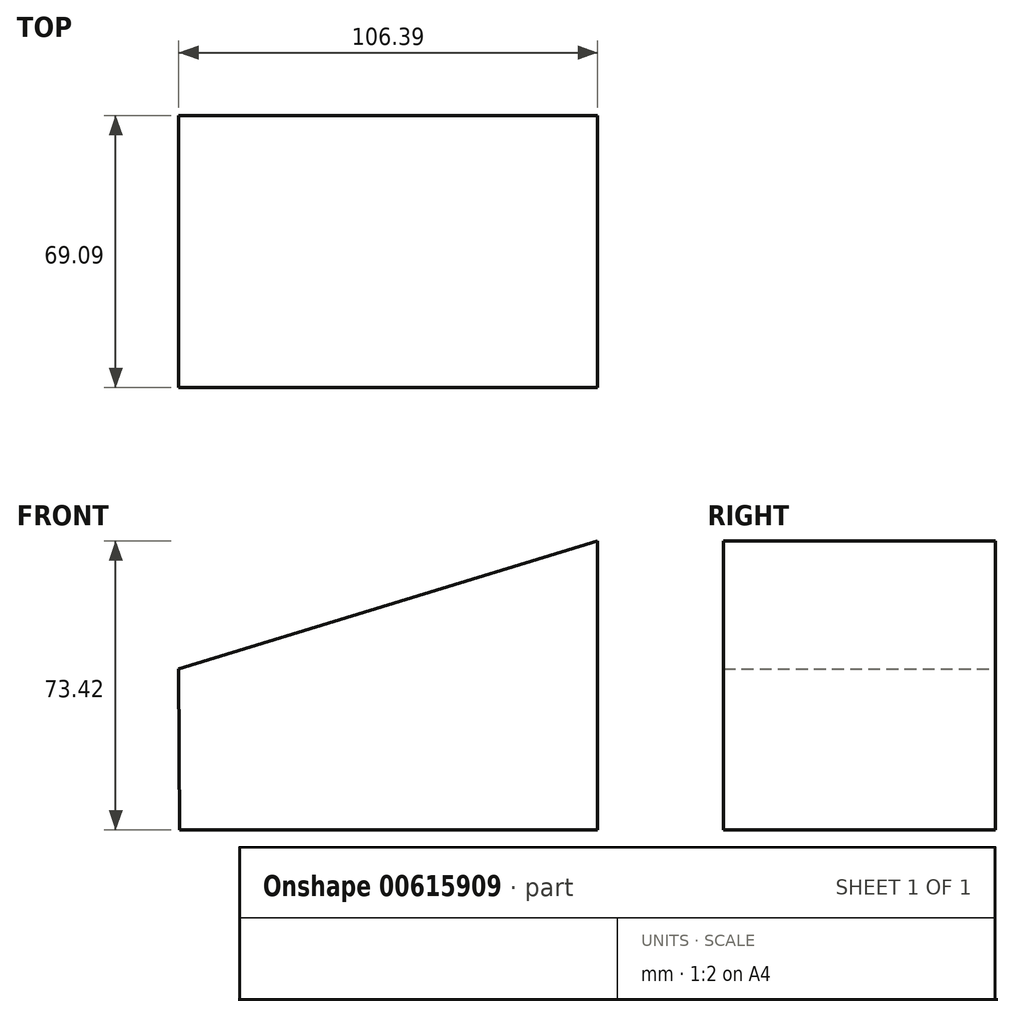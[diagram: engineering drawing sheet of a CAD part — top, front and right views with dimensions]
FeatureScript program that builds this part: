
annotation { "Feature Type Name" : "Feature", "Feature Type Description" : "" }
export const myFeature = defineFeature(function(context is Context, id is Id, definition is map)
    precondition{}
    {
        {
            var Q0;
            Q0=qCreatedBy(makeId("Front.planeOp"),FACE);
            var sketch = newSketch(context, id + "F0", { "sketchPlane" : qUnion([Q0])});
            skLineSegment(sketch, "E0", {"start": v(-59.68, 46.93) * mm, "end": v(46.7, 79.46) * mm});
            skLineSegment(sketch, "E1", {"start": v(46.7, 79.46) * mm, "end": v(46.7, 6.04) * mm});
            skLineSegment(sketch, "E2", {"start": v(46.7, 6.04) * mm, "end": v(-59.46, 6.04) * mm});
            skLineSegment(sketch, "E3", {"start": v(-59.46, 6.04) * mm, "end": v(-59.68, 46.93) * mm});
            skSolve(sketch);
        }
        {
            var Q0;
            Q0=makeQuery(id+"F0.imprint","IMPRINT",FACE,{"disambiguationData":[TD([[makeQuery(id+"F0.imprint","IMPRINT",EDGE,{"derivedFrom":sQuery(id+"F0.wireOp",EDGE,"E0")}),-1.0]])]});
            extrude(context, id + "F1", {"entities" : qUnion([Q0]), "depth" : 69.1 * mm, "offsetDistance" : 25.4 * mm});
        }
    });
